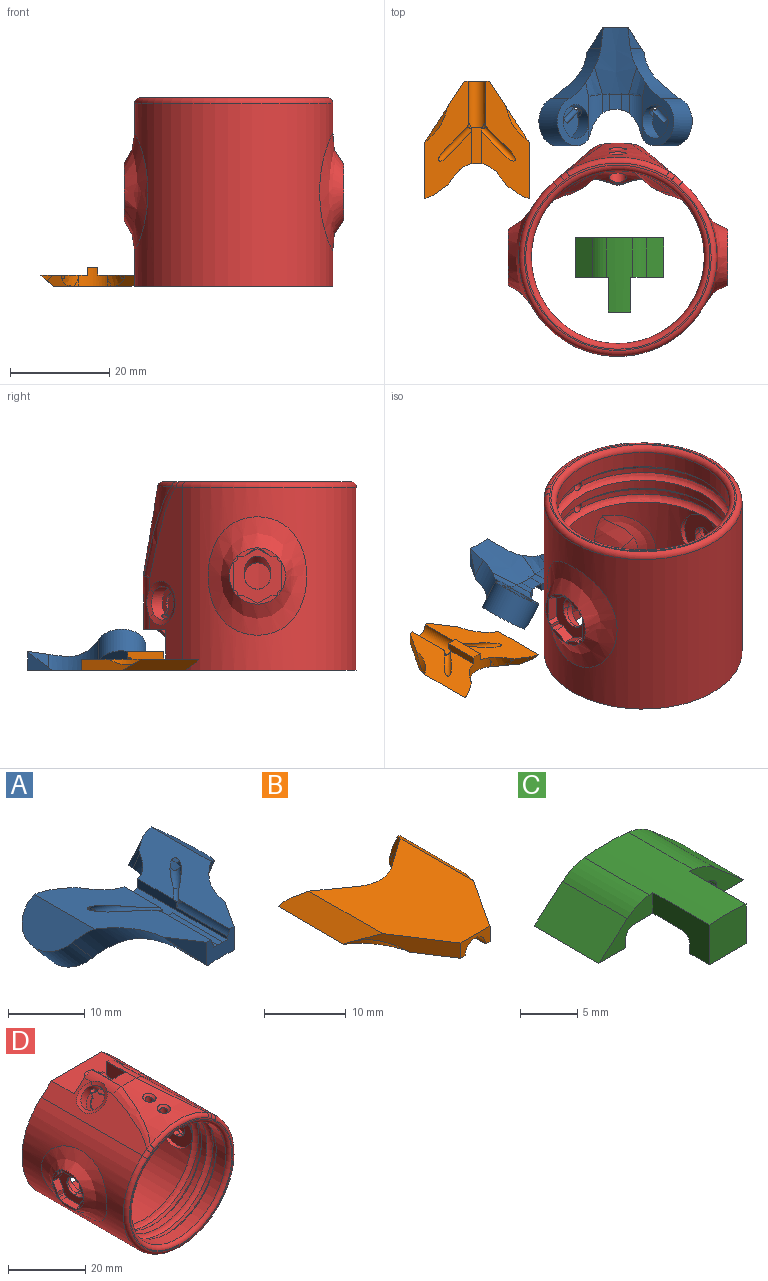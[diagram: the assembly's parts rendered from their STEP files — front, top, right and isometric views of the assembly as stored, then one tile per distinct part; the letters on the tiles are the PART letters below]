
ASSEMBLY  parts=4 mates=3
PART A: 51 faces, bbox 31.1x24x11.9 mm
  f0: cylinder r=1.78mm len=9.4mm, axis (0,-1,0), area 10.4mm2, adj f10,f35,f45,f48,f49
  f1: cylinder r=1.78mm len=9.4mm, axis (0,-1,0), area 10.4mm2, adj f2,f10,f43,f46,f47
  f2: plane 1.03x0.65mm, normal (0,-1,0), area 0.3mm2, adj f1,f40,f43,f46,f47
  f3: plane 0.95x0.07mm, normal (0,-1,0), area 0mm2, adj f34,f50
  f4: cylinder r=5.08mm len=8.88mm, axis (0,-1,0), area 18.1mm2, adj f6,f20,f21,f29,f32
  f5: cylinder r=5.08mm len=8.88mm, axis (0,-1,0), area 18.1mm2, adj f6,f23,f24,f30,f31
  f6: cylinder r=23.18mm len=5.47mm, axis (0,-1,0), area 18mm2, adj f4,f5,f20,f22,f24,f31,f32,f33
  f7: plane 2.14x1.83mm, normal (0.52,0.73,0.45), area 2.4mm2, adj f8,f29,f48
  f8: cylinder r=4.93mm len=10.03mm, axis (-0.65,0,0.76), area 96.2mm2, adj f7,f11,f13,f21,f29,f48
  f9: plane 2.14x1.83mm, normal (-0.52,0.73,0.45), area 2.4mm2, adj f15,f30,f46
  f10: plane 5.08x3.82mm, normal (0,-1,0), area 14.6mm2, adj f0,f1,f12,f16,f18,f19,f22,f34
  f11: plane 11.29x4.61mm, normal (-0.65,0,0.76), area 50.7mm2, adj f8,f13,f48
  f12: plane 4.18x3.27mm, normal (-0.76,0,-0.65), area 7.5mm2, adj f10,f13,f19,f22
  f13: cylinder r=11.01mm len=10.23mm, axis (-0.65,0,0.76), area 59.7mm2, adj f8,f11,f12,f19,f20,f21,f22,f48
  f14: plane 11.29x4.61mm, normal (0.65,0,0.76), area 50.7mm2, adj f15,f17,f46
  f15: cylinder r=4.93mm len=10.03mm, axis (0.65,0,0.76), area 96.3mm2, adj f9,f14,f17,f23,f30,f46
  f16: plane 4.2x3.28mm, normal (0.76,0,-0.65), area 7.6mm2, adj f10,f17,f18,f22
  f17: cylinder r=10.99mm len=10.23mm, axis (0.65,0,0.76), area 59.6mm2, adj f14,f15,f16,f18,f22,f23,f24,f46
  f18: plane 4.98x3.75mm, normal (0.84,-0.55,0), area 11mm2, adj f10,f16,f17,f46
  f19: plane 4.98x3.75mm, normal (-0.84,-0.55,0), area 11mm2, adj f10,f12,f13,f48
  f20: bspline ~12.9x5.76mm, area 12.6mm2, adj f4,f6,f13,f21,f22
  f21: plane 12.77x6.34mm, normal (0.65,0,-0.76), area 39.7mm2, adj f4,f8,f13,f20,f25,f29
  f22: cone r=20.13mm half-angle=9.1deg, axis (0,1,0), area 89.6mm2, adj f6,f10,f12,f13,f16,f17,f20,f24
  f23: plane 12.77x6.34mm, normal (-0.65,0,-0.76), area 39.7mm2, adj f5,f15,f17,f24,f27,f30
  f24: bspline ~11.39x5.36mm, area 12.6mm2, adj f5,f6,f17,f22,f23
  f25: cylinder r=3.4mm len=7.24mm, axis (0.65,0,-0.76), area 64mm2, adj f21,f26,f44
  f26: plane 6.97x5.41mm, normal (0.65,0,-0.76), area 17.5mm2, adj f25,f36,f37,f38,f44
  f27: cylinder r=3.4mm len=7.24mm, axis (-0.65,0,-0.76), area 64mm2, adj f23,f28,f42
  f28: plane 6.97x5.41mm, normal (-0.65,0,-0.76), area 32mm2, adj f27,f39,f40,f41,f42
  f29: bspline ~3.9x2.82mm, area 4.5mm2, adj f4,f7,f8,f21,f32,f48
  f30: bspline ~3.9x2.82mm, area 4.5mm2, adj f5,f9,f15,f23,f31,f46
  f31: bspline ~6.38x4.93mm, area 9.7mm2, adj f5,f6,f30,f33,f46
  f32: bspline ~6.14x4.86mm, area 9.7mm2, adj f4,f6,f29,f33,f48
  f33: cylinder r=5.08mm len=5.59mm, axis (0,0,1), area 5.6mm2, adj f6,f31,f32,f46,f47,f48,f49,f50
  f34: cylinder r=1.78mm len=9.4mm, axis (0,-1,0), area 9.1mm2, adj f3,f10,f50
  f35: plane 1.03x0.65mm, normal (0,-1,0), area 0.3mm2, adj f0,f37,f45,f48,f49
  f36: plane 1.25x1.2mm, normal (0.59,-0.64,0.5), area 1.5mm2, adj f26,f37,f38
  f37: torus R=23.24mm, axis (0.7,0.71,0.08), area 26.5mm2, adj f26,f35,f36,f38,f44,f48,f49
  f38: torus R=23.24mm, axis (0.7,0.71,0.08), area 0.7mm2, adj f26,f36,f37
  f39: plane 1.25x1.2mm, normal (-0.59,-0.64,0.5), area 1.5mm2, adj f28,f40,f41
  f40: torus R=23.24mm, axis (0.7,-0.71,-0.08), area 25.4mm2, adj f2,f28,f39,f41,f42,f46,f47
  f41: torus R=23.24mm, axis (0.7,-0.71,-0.08), area 0.7mm2, adj f28,f39,f40
  f42: bspline ~2.29x2.29mm, area 4.9mm2, adj f27,f28,f40
  f43: bspline ~1.31x0.88mm, area 0.1mm2, adj f1,f2,f46
  f44: bspline ~2.33x2.29mm, area 4.9mm2, adj f25,f26,f37
  f45: bspline ~1.37x0.92mm, area 0.1mm2, adj f0,f35,f48
  f46: plane 23.88x9.75mm, normal (0,0,1), area 123.2mm2, adj f1,f2,f9,f10,f14,f15,f17,f18
  f47: plane 16.65x1.47mm, normal (-1,0,0), area 14.9mm2, adj f1,f2,f10,f33,f40,f46,f50
  f48: plane 23.88x9.75mm, normal (0,0,1), area 123.3mm2, adj f0,f7,f8,f10,f11,f13,f19,f29
  f49: plane 16.65x1.47mm, normal (1,0,0), area 14.9mm2, adj f0,f10,f33,f35,f37,f48,f50
  f50: plane 16.64x2.54mm, normal (0,0,1), area 33mm2, adj f3,f10,f33,f34,f47,f49
PART B: 32 faces, bbox 22.2x24.7x7.9 mm
  f0: plane 1.59x0.85mm, normal (-0.58,0.81,0), area 0.8mm2, adj f1,f19,f21
  f1: plane 20.97x15.81mm, normal (0,0,1), area 245mm2, adj f0,f2,f3,f5,f7,f9,f18,f19
  f2: plane 1.59x0.85mm, normal (0.58,0.81,0), area 0.8mm2, adj f1,f19,f20
  f3: plane 11.33x7.38mm, normal (-0.84,-0.55,0), area 21.8mm2, adj f1,f4,f5,f18,f31
  f4: cylinder r=11.01mm len=6.87mm, axis (-0.65,0,0.76), area 5mm2, adj f3,f5,f31
  f5: plane 15.39x2.67mm, normal (-0.65,0,0.76), area 43mm2, adj f1,f3,f4,f25,f26,f31
  f6: cylinder r=4.93mm len=2.44mm, axis (0.65,0,0.76), area 1.7mm2, adj f9,f24,f30
  f7: plane 11.33x7.37mm, normal (0.84,-0.55,0), area 21.8mm2, adj f1,f8,f9,f18,f30
  f8: cylinder r=10.99mm len=6.87mm, axis (0.65,0,0.76), area 5mm2, adj f7,f9,f30
  f9: plane 15.39x2.67mm, normal (0.65,0,0.76), area 43mm2, adj f1,f6,f7,f8,f24,f30
  f10: bspline ~1.79x1.24mm, area 1.2mm2, adj f11,f14,f16,f17,f31
  f11: torus R=23.24mm, axis (0.7,0.71,0.08), area 25.1mm2, adj f10,f14,f16,f28,f31
  f12: bspline ~1.82x1.32mm, area 1.2mm2, adj f13,f14,f15,f17,f30
  f13: torus R=23.24mm, axis (0.7,-0.71,-0.08), area 25.1mm2, adj f12,f14,f15,f29,f30
  f14: plane 3.4x3.29mm, normal (0,-1,0), area 4.4mm2, adj f10,f11,f12,f13,f17,f27,f28,f29
  f15: plane 0.07x0.06mm, normal (0,-1,0), area 0mm2, adj f12,f13,f30
  f16: plane 0.06x0.05mm, normal (0,-1,0), area 0mm2, adj f10,f11,f31
  f17: cylinder r=1.78mm len=9.4mm, axis (0,-1,0), area 51.2mm2, adj f10,f12,f14,f18,f30,f31
  f18: plane 5.08x2.29mm, normal (0,-1,0), area 6.6mm2, adj f1,f3,f7,f17,f30,f31
  f19: cylinder r=5.08mm len=5.91mm, axis (0,0,1), area 17.3mm2, adj f0,f1,f2,f20,f21,f27,f28,f29
  f20: bspline ~6.23x4.58mm, area 8mm2, adj f2,f19,f23,f26,f31
  f21: bspline ~6.79x4.93mm, area 8mm2, adj f0,f19,f22,f24,f30
  f22: bspline ~1.23x1.08mm, area 0.7mm2, adj f21,f24,f30
  f23: bspline ~1.23x1.08mm, area 0.7mm2, adj f20,f26,f31
  f24: plane 5.37x4.5mm, normal (-0.52,0.73,0.45), area 8.6mm2, adj f1,f6,f9,f21,f22,f30
  f25: cylinder r=4.93mm len=2.44mm, axis (-0.65,0,0.76), area 1.7mm2, adj f5,f26,f31
  f26: plane 5.37x4.5mm, normal (0.52,0.73,0.45), area 8.6mm2, adj f1,f5,f20,f23,f25,f31
  f27: plane 7.18x2.03mm, normal (0,0,-1), area 14.5mm2, adj f14,f19,f28,f29
  f28: plane 7.24x1.51mm, normal (-1,0,0), area 10.3mm2, adj f11,f14,f19,f27,f31
  f29: plane 7.24x1.51mm, normal (1,0,0), area 10.3mm2, adj f13,f14,f19,f27,f30
  f30: plane 24.7x10.63mm, normal (0,0,-1), area 120.6mm2, adj f6,f7,f8,f9,f12,f13,f15,f17
  f31: plane 24.69x10.62mm, normal (0,0,-1), area 121mm2, adj f3,f4,f5,f10,f11,f16,f17,f18
PART C: 22 faces, bbox 17.9x15x4.4 mm
  f0: plane 4.51x2.42mm, normal (0,0,-1), area 10.9mm2, adj f1,f10,f11,f14
  f1: plane 6.99x4.26mm, normal (1,0,0), area 20.7mm2, adj f0,f9,f11,f12,f14,f17,f21
  f2: plane 6.69x4.26mm, normal (0,-1,0), area 10.9mm2, adj f4,f6,f8,f9,f10,f15,f17,f20
  f3: plane 17.89x4.37mm, normal (0,1,0), area 54.5mm2, adj f4,f5,f6,f7,f8,f9
  f4: cylinder r=5.08mm len=8mm, axis (0,-1,0), area 24mm2, adj f2,f3,f8,f9
  f5: cylinder r=5.08mm len=8mm, axis (0,-1,0), area 24mm2, adj f3,f7,f9,f12
  f6: plane 17.89x8mm, normal (0,0,-1), area 70mm2, adj f2,f3,f7,f8,f12,f13,f15,f16
  f7: plane 8x3.52mm, normal (0.65,0,0.76), area 37.1mm2, adj f3,f5,f6,f12
  f8: plane 8x3.52mm, normal (-0.65,0,0.76), area 37.1mm2, adj f2,f3,f4,f6
  f9: cylinder r=23.05mm len=14.99mm, axis (0,-1,0), area 75.1mm2, adj f1,f2,f3,f4,f5,f10,f11,f12
  f10: plane 6.99x4.26mm, normal (-1,0,0), area 20.7mm2, adj f0,f2,f9,f11,f14,f17,f21
  f11: plane 4.51x4.37mm, normal (0,-1,0), area 19.6mm2, adj f0,f1,f9,f10
  f12: plane 6.69x4.26mm, normal (0,-1,0), area 10.9mm2, adj f1,f5,f6,f7,f9,f13,f17,f18
  f13: plane 6.51x1.02mm, normal (-1,0,0), area 6.6mm2, adj f6,f12,f16,f18
  f14: plane 4.51x1.02mm, normal (0,1,0), area 4.6mm2, adj f0,f1,f10,f21
  f15: plane 6.51x1.02mm, normal (1,0,0), area 6.6mm2, adj f2,f6,f16,f20
  f16: plane 11.22x1.02mm, normal (0,-1,0), area 11.4mm2, adj f6,f13,f15,f19
  f17: plane 9.18x9.05mm, normal (0,0,-1), area 66.5mm2, adj f1,f2,f10,f12,f18,f19,f20,f21
  f18: cylinder r=1.02mm len=6.51mm, axis (0,-1,0), area 9.8mm2, adj f12,f13,f17,f19
  f19: cylinder r=1.02mm len=11.22mm, axis (1,0,0), area 16.7mm2, adj f16,f17,f18,f20
  f20: cylinder r=1.02mm len=6.51mm, axis (0,1,0), area 9.8mm2, adj f2,f15,f17,f19
  f21: cylinder r=1.02mm len=4.51mm, axis (-1,0,0), area 7.2mm2, adj f1,f10,f14,f17
PART D: 145 faces, bbox 46.1x39x46.2 mm
  f0: plane 6.85x5.02mm, normal (0,0,1), area 24.9mm2, adj f1,f2,f3,f4
  f1: plane 6.99x4.44mm, normal (-1,0,0), area 31mm2, adj f0,f2,f4,f5,f6
  f2: cylinder r=2.69mm len=5.37mm, axis (0,0.75,0.66), area 14.6mm2, adj f0,f1,f3,f6,f7,f8,f9
  f3: plane 6.99x4.44mm, normal (1,0,0), area 31mm2, adj f0,f2,f4,f5,f9
  f4: plane 5.02x4.57mm, normal (0,1,0), area 22.7mm2, adj f0,f1,f3,f5
  f5: cylinder r=23.05mm len=10.8mm, axis (0,-1,0), area 23.6mm2, adj f1,f3,f4,f6,f9,f10,f11,f12
  f6: plane 6.67x4.44mm, normal (0,1,0), area 15.5mm2, adj f1,f2,f5,f7,f14,f15,f16
  f7: plane 18.39x8.28mm, normal (0,0,1), area 132.1mm2, adj f2,f6,f8,f9,f15,f17,f18,f19
  f8: cone r=0.03mm half-angle=45deg, axis (0,-0.75,-0.66), area 4.5mm2, adj f2,f7,f19
  f9: plane 6.67x4.44mm, normal (0,1,0), area 15.5mm2, adj f2,f3,f5,f7,f10,f17,f20
  f10: cylinder r=5.08mm len=10.79mm, axis (0,-1,0), area 27.5mm2, adj f5,f9,f11,f17,f21
  f11: bspline ~24.13x10.56mm, area 46.4mm2, adj f5,f10,f12,f17,f22
  f12: cone r=20mm half-angle=9.1deg, axis (0,1,0), area 235.7mm2, adj f5,f11,f13,f23,f24,f25
  f13: bspline ~23.12x10.29mm, area 46.4mm2, adj f5,f12,f14,f15,f26
  f14: cylinder r=5.08mm len=10.79mm, axis (0,-1,0), area 27.5mm2, adj f5,f6,f13,f15,f27
  f15: plane 36.96x7.6mm, normal (0.65,0,0.76), area 211.5mm2, adj f6,f7,f13,f14,f18,f28,f29,f30
  f16: cylinder r=0.76mm len=3.96mm, axis (0.43,-0.82,-0.37), area 15.1mm2, adj f6,f31,f32,f33,f34
  f17: plane 36.96x7.6mm, normal (-0.65,0,0.76), area 211.5mm2, adj f7,f9,f10,f11,f18,f30,f35,f36
  f18: plane 40.01x38.48mm, normal (0,1,0), area 286.2mm2, adj f7,f15,f17,f30,f37
  f19: cylinder r=2.29mm len=5.29mm, axis (0,0.75,0.66), area 16.3mm2, adj f7,f8,f38
  f20: cylinder r=0.76mm len=3.87mm, axis (-0.42,-0.83,-0.36), area 14.6mm2, adj f9,f39,f40,f41,f42
  f21: bspline ~5.66x1.42mm, area 6.2mm2, adj f10,f36,f39
  f22: bspline ~3.41x2.66mm, area 2.5mm2, adj f11,f25,f35,f43
  f23: bspline ~3.47x3.36mm, area 8.3mm2, adj f12,f44
  f24: bspline ~3.46x3.36mm, area 8.3mm2, adj f12,f45
  f25: torus R=19.03mm, axis (0,-1,0), area 34.3mm2, adj f12,f22,f26,f43
  f26: bspline ~2.42x2.17mm, area 2.5mm2, adj f13,f25,f29,f43
  f27: bspline ~5.66x1.42mm, area 6.2mm2, adj f14,f28,f31
  f28: cone r=3.43mm half-angle=69.4deg, axis (0.65,0,0.76), area 20.9mm2, adj f15,f27,f31
  f29: cylinder r=1.14mm len=2.17mm, axis (-0.76,0,0.65), area 3.4mm2, adj f15,f26,f43,f46
  f30: cylinder r=20mm len=40.01mm, axis (0,-1,0), area 3200.1mm2, adj f15,f17,f18,f46,f47
  f31: cylinder r=3.43mm len=7.11mm, axis (0.65,0,0.76), area 61.3mm2, adj f16,f27,f28,f32,f34,f48
  f32: plane 0.33x0.28mm, normal (0.65,0,0.76), area 0mm2, adj f16,f31,f33
  f33: plane 1.6x1.47mm, normal (0.43,-0.82,-0.37), area 0.8mm2, adj f16,f32,f34,f49,f50,f51
  f34: plane 0.34x0.28mm, normal (0.65,0,0.76), area 0mm2, adj f16,f31,f33
  f35: cylinder r=1.14mm len=2.17mm, axis (0.76,0,0.65), area 3.4mm2, adj f17,f22,f43,f46
  f36: cone r=3.43mm half-angle=69.4deg, axis (-0.65,0,0.76), area 20.9mm2, adj f17,f21,f39
  f37: cylinder r=17.46mm len=34.93mm, axis (0,-1,0), area 2086.9mm2, adj f18,f52,f53,f54,f55,f56,f57,f58
  f38: plane 4.57x3.43mm, normal (0,0.75,0.66), area 7.2mm2, adj f19,f63
  f39: cylinder r=3.43mm len=7.11mm, axis (-0.65,0,0.76), area 61mm2, adj f20,f21,f36,f40,f42,f64
  f40: plane 0.34x0.28mm, normal (-0.65,0,0.76), area 0mm2, adj f20,f39,f41
  f41: plane 1.62x1.49mm, normal (-0.42,-0.83,-0.36), area 0.8mm2, adj f20,f40,f42,f65,f66,f67
  f42: plane 0.33x0.28mm, normal (-0.65,0,0.76), area 0mm2, adj f20,f39,f41
  f43: plane 37.89x37.72mm, normal (0,-1,0), area 33.8mm2, adj f22,f25,f26,f29,f35,f46,f68
  f44: cylinder r=1.02mm len=2.2mm, axis (0,0,-1), area 11.3mm2, adj f23,f69,f70,f71
  f45: cylinder r=1.02mm len=3.06mm, axis (0,0,-1), area 16.7mm2, adj f24,f54,f72,f73
  f46: torus R=18.86mm, axis (0,-1,0), area 171.1mm2, adj f29,f30,f35,f43
  f47: bspline ~23.89x19.93mm, area 346mm2, adj f30,f74
  f48: plane 6.86x5.21mm, normal (0.65,0,0.76), area 18.8mm2, adj f31,f49,f51,f75
  f49: plane 1.05x0.89mm, normal (0.62,0.57,-0.53), area 0.7mm2, adj f33,f48,f50,f75
  f50: plane 5.5x3.75mm, normal (0.65,0,0.76), area 18mm2, adj f33,f49,f51,f75
  f51: plane 1.05x0.89mm, normal (-0.62,-0.57,0.53), area 0.7mm2, adj f33,f48,f50,f75
  f52: cylinder r=5.68mm len=11.37mm, axis (1,0,0), area 21.4mm2, adj f37,f76
  f53: cylinder r=5.68mm len=11.37mm, axis (1,0,0), area 21.4mm2, adj f37,f77
  f54: torus R=16.95mm, axis (0,-1,0), area 190.2mm2, adj f37,f45,f73
  f55: bspline ~9.99x8.89mm, area 40.2mm2, adj f37,f56,f62,f78
  f56: bspline ~18.53x11.81mm, area 69.1mm2, adj f37,f55,f57,f78,f79
  f57: bspline ~17.69x8.92mm, area 56.3mm2, adj f37,f56,f58,f79,f80,f81,f82,f83
  f58: bspline ~18.53x11.81mm, area 69.1mm2, adj f37,f57,f59,f83,f84
  f59: bspline ~10.56x8.87mm, area 40.2mm2, adj f37,f58,f60,f84
  f60: plane 6.54x2.81mm, normal (-0.65,0,-0.76), area 12.9mm2, adj f37,f59,f61,f83
  f61: bspline ~13.07x6.34mm, area 35.3mm2, adj f37,f60,f62,f63,f79,f80,f82,f83
  f62: plane 6.54x2.81mm, normal (0.65,0,-0.76), area 12.9mm2, adj f37,f55,f61,f79
  f63: cylinder r=1.71mm len=5.19mm, axis (0,0.75,0.66), area 42mm2, adj f38,f61
  f64: plane 6.86x5.21mm, normal (-0.65,0,0.76), area 18.1mm2, adj f39,f65,f67,f88
  f65: plane 1.02x0.85mm, normal (0.63,-0.55,0.54), area 0.6mm2, adj f41,f64,f66,f88
  f66: plane 5.58x3.75mm, normal (-0.65,0,0.76), area 18.6mm2, adj f41,f65,f67,f88
  f67: plane 1.02x0.85mm, normal (-0.63,0.55,-0.54), area 0.6mm2, adj f41,f64,f66,f88
  f68: torus R=18.61mm, axis (0,-1,0), area 201.7mm2, adj f43,f89
  f69: torus R=16.95mm, axis (0,-1,0), area 190.2mm2, adj f44,f70,f89
  f70: cylinder r=18.63mm len=37.26mm, axis (0,-1,0), area 136.7mm2, adj f44,f69,f71
  f71: torus R=16.95mm, axis (0,-1,0), area 190.2mm2, adj f44,f70,f90
  f72: torus R=16.95mm, axis (0,-1,0), area 190.2mm2, adj f45,f73,f90
  f73: cylinder r=18.63mm len=37.26mm, axis (0,-1,0), area 136.7mm2, adj f45,f54,f72
  f74: plane 12.17x12.17mm, normal (-1,0,0), area 18.3mm2, adj f47,f91,f92,f93,f94,f95,f96,f97
  f75: cylinder r=2.24mm len=4.47mm, axis (0.65,0,0.76), area 6.1mm2, adj f48,f49,f50,f51
  f76: plane 11.37x11.37mm, normal (1,0,0), area 72.5mm2, adj f52,f111,f112
  f77: plane 11.37x11.37mm, normal (-1,0,0), area 72.5mm2, adj f53,f113,f114
  f78: bspline ~6.25x4.79mm, area 12.2mm2, adj f55,f56,f79
  f79: bspline ~8.86x8.83mm, area 30.1mm2, adj f56,f57,f61,f62,f78,f80
  f80: bspline ~5.7x2.92mm, area 2.6mm2, adj f57,f61,f79,f86
  f81: cylinder r=2.69mm len=2.75mm, axis (0,0.75,0.66), area 4.2mm2, adj f57,f86,f87,f115
  f82: bspline ~5.36x2.76mm, area 2.6mm2, adj f57,f61,f83,f87
  f83: bspline ~9.05x8.88mm, area 30mm2, adj f57,f58,f60,f61,f82,f84
  f84: bspline ~6.25x4.79mm, area 12.2mm2, adj f58,f59,f83
  f85: plane 1.46x0.12mm, normal (0,-0.75,-0.66), area 0.2mm2, adj f61,f115
  f86: bspline ~1.6x1.09mm, area 0.4mm2, adj f61,f80,f81,f115
  f87: bspline ~1.6x1.09mm, area 0.4mm2, adj f61,f81,f82,f115
  f88: cylinder r=2.29mm len=4.57mm, axis (-0.65,0,0.76), area 6.2mm2, adj f64,f65,f66,f67
  f89: cylinder r=17.46mm len=34.93mm, axis (0,-1,0), area 382.1mm2, adj f68,f69
  f90: cylinder r=17.46mm len=34.93mm, axis (0,-1,0), area 211.3mm2, adj f71,f72
  f91: plane 3.57x3.01mm, normal (0,0.87,0.5), area 6.3mm2, adj f74,f92,f93,f109,f116
  f92: cylinder r=2.67mm len=1.72mm, axis (-0.83,-0.56,0), area 0mm2, adj f74,f91
  f93: plane 2.16x1.28mm, normal (0,1,0), area 2.8mm2, adj f74,f91,f94,f116
  f94: plane 2.16x0.74mm, normal (0,0,1), area 1.6mm2, adj f74,f93,f95,f116
  f95: plane 2.16x0.83mm, normal (0,0.87,0.5), area 2.1mm2, adj f74,f94,f96,f116
  f96: plane 5.57x2.16mm, normal (0,0,1), area 12mm2, adj f74,f95,f97,f116
  f97: plane 2.16x0.83mm, normal (0,-0.87,0.5), area 2.1mm2, adj f74,f96,f98,f116
  f98: plane 2.16x0.74mm, normal (0,0,1), area 1.6mm2, adj f74,f97,f99,f116
  f99: plane 2.16x1.28mm, normal (0,-1,0), area 2.8mm2, adj f74,f98,f100,f116
  f100: plane 2.72x2.16mm, normal (0,-0.87,0.5), area 6.8mm2, adj f74,f99,f101,f116
  f101: plane 2.72x2.16mm, normal (0,-0.87,-0.5), area 6.8mm2, adj f74,f100,f102,f116
  f102: plane 2.16x1.28mm, normal (0,-1,0), area 2.8mm2, adj f74,f101,f103,f116
  f103: plane 2.16x0.74mm, normal (0,0,-1), area 1.6mm2, adj f74,f102,f104,f116
  f104: plane 2.16x0.83mm, normal (0,-0.87,-0.5), area 2.1mm2, adj f74,f103,f105,f116
  f105: plane 5.57x2.16mm, normal (0,0,-1), area 12mm2, adj f74,f104,f106,f116
  f106: plane 2.16x0.83mm, normal (0,0.87,-0.5), area 2.1mm2, adj f74,f105,f107,f116
  f107: plane 2.16x0.74mm, normal (0,0,-1), area 1.6mm2, adj f74,f106,f108,f116
  f108: plane 2.16x1.28mm, normal (0,1,0), area 2.8mm2, adj f74,f107,f109,f116
  f109: plane 3.35x2.79mm, normal (0,0.87,-0.5), area 6.3mm2, adj f74,f91,f108,f110,f116
  f110: cylinder r=2.67mm len=1.72mm, axis (-0.83,-0.56,0), area 0mm2, adj f74,f109
  f111: cylinder r=2.67mm len=5.33mm, axis (-0.83,-0.56,0), area 17.9mm2, adj f76,f112,f117
  f112: cylinder r=2.67mm len=5.33mm, axis (1,0,0), area 6.2mm2, adj f76,f111,f118
  f113: cylinder r=2.67mm len=5.33mm, axis (1,0,0), area 6.2mm2, adj f77,f114,f119
  f114: cylinder r=2.67mm len=5.33mm, axis (0.83,-0.56,0), area 17.9mm2, adj f77,f113,f120
  f115: torus R=2.18mm, axis (0,0.75,0.66), area 1.4mm2, adj f81,f85,f86,f87
  f116: plane 11.15x9.65mm, normal (-1,0,0), area 53.7mm2, adj f91,f93,f94,f95,f96,f97,f98,f99
  f117: cylinder r=2.67mm len=5.33mm, axis (1,0,0), area 6.2mm2, adj f111,f116,f118
  f118: cylinder r=2.67mm len=5.33mm, axis (-0.83,-0.56,0), area 17.9mm2, adj f112,f116,f117
  f119: cylinder r=2.67mm len=5.33mm, axis (0.83,-0.56,0), area 17.9mm2, adj f113,f120,f121
  f120: cylinder r=2.67mm len=5.33mm, axis (1,0,0), area 6.2mm2, adj f114,f119,f121
  f121: plane 11.15x9.65mm, normal (1,0,0), area 53.7mm2, adj f119,f120,f122,f123,f124,f125,f126,f127
  f122: plane 2.16x1.28mm, normal (0,1,0), area 2.8mm2, adj f121,f123,f139,f140
  f123: plane 3.57x3.01mm, normal (0,0.87,-0.5), area 6.3mm2, adj f121,f122,f124,f140,f141
  f124: plane 3.35x2.79mm, normal (0,0.87,0.5), area 6.3mm2, adj f121,f123,f125,f140,f142
  f125: plane 2.16x1.28mm, normal (0,1,0), area 2.8mm2, adj f121,f124,f126,f140
  f126: plane 2.16x0.74mm, normal (0,0,1), area 1.6mm2, adj f121,f125,f127,f140
  f127: plane 2.16x0.83mm, normal (0,0.87,0.5), area 2.1mm2, adj f121,f126,f128,f140
  f128: plane 5.57x2.16mm, normal (0,0,1), area 12mm2, adj f121,f127,f129,f140
  f129: plane 2.16x0.83mm, normal (0,-0.87,0.5), area 2.1mm2, adj f121,f128,f130,f140
  f130: plane 2.16x0.74mm, normal (0,0,1), area 1.6mm2, adj f121,f129,f131,f140
  f131: plane 2.16x1.28mm, normal (0,-1,0), area 2.8mm2, adj f121,f130,f132,f140
  f132: plane 2.72x2.16mm, normal (0,-0.87,0.5), area 6.8mm2, adj f121,f131,f133,f140
  f133: plane 2.72x2.16mm, normal (0,-0.87,-0.5), area 6.8mm2, adj f121,f132,f134,f140
  f134: plane 2.16x1.28mm, normal (0,-1,0), area 2.8mm2, adj f121,f133,f135,f140
  f135: plane 2.16x0.74mm, normal (0,0,-1), area 1.6mm2, adj f121,f134,f136,f140
  f136: plane 2.16x0.83mm, normal (0,-0.87,-0.5), area 2.1mm2, adj f121,f135,f137,f140
  f137: plane 5.57x2.16mm, normal (0,0,-1), area 12mm2, adj f121,f136,f138,f140
  f138: plane 2.16x0.83mm, normal (0,0.87,-0.5), area 2.1mm2, adj f121,f137,f139,f140
  f139: plane 2.16x0.74mm, normal (0,0,-1), area 1.6mm2, adj f121,f122,f138,f140
  f140: plane 12.17x12.17mm, normal (1,0,0), area 18.4mm2, adj f122,f123,f124,f125,f126,f127,f128,f129
  f141: cylinder r=2.67mm len=1.72mm, axis (0.83,-0.56,0), area 0mm2, adj f123,f140
  f142: cylinder r=2.67mm len=1.72mm, axis (0.83,-0.56,0), area 0mm2, adj f124,f140
  f143: bspline ~23.89x19.93mm, area 348.7mm2, adj f140,f144
  f144: cylinder r=20mm len=23.89mm, axis (0,-1,0), area 396.5mm2, adj f143
PLACE A rot(axis=(-1,0,0),180deg) t=(-23.42,54.04,18.4)mm
PLACE B rot(axis=(-1,0,0),180deg) t=(-51.44,43.19,20.94)mm
PLACE C t=(-22.62,-32.08,-24.98)mm
PLACE D rot(axis=(-1,0,0),90deg) t=(-22.98,2.07,31.8)mm
MATE planar A.f46 <-> D.f18  axis (0,0,-1) through (-17.55,35.32,-6.3)mm
MATE planar B.f1 <-> D.f18  axis (0,0,-1) through (-51.44,27.23,-6.3)mm
MATE planar C.f6 <-> B.f1  axis (0,0,-1) through (-22.64,2.8,-6.3)mm
